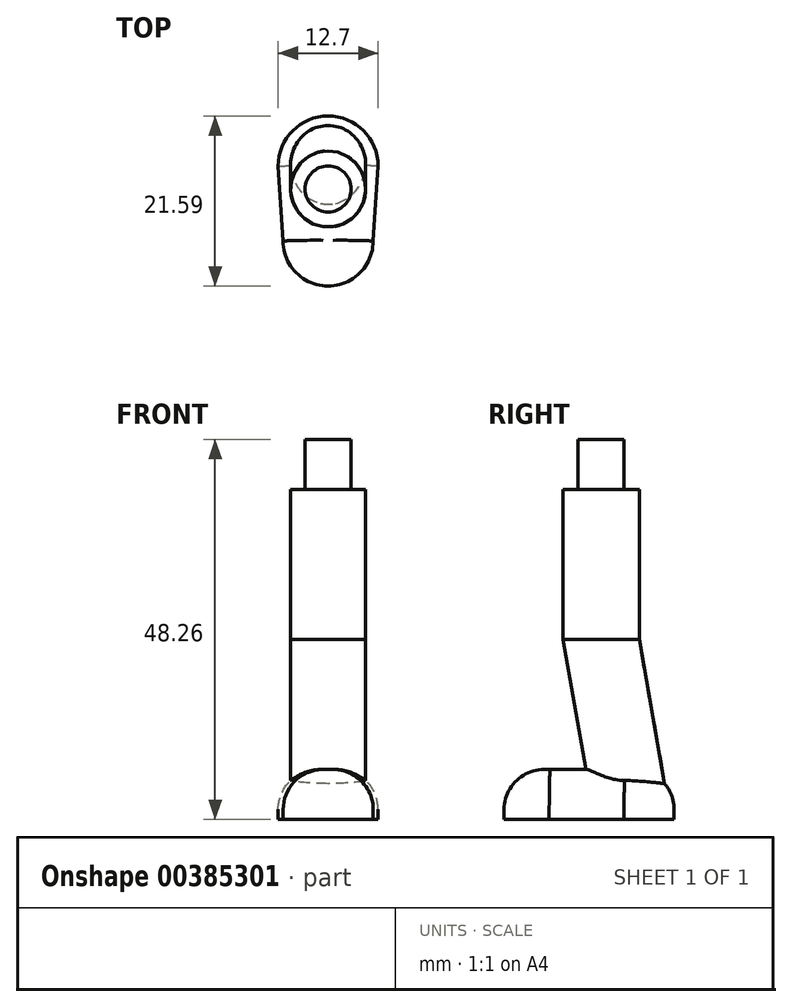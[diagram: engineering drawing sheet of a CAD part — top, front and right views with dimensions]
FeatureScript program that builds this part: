
annotation { "Feature Type Name" : "Feature", "Feature Type Description" : "" }
export const myFeature = defineFeature(function(context is Context, id is Id, definition is map)
    precondition{}
    {
        {
            var Q0;
            Q0=qCreatedBy(makeId("Top.planeOp"),FACE);
            var sketch = newSketch(context, id + "F0", { "sketchPlane" : qUnion([Q0])});
            skArc(sketch, "E0", {"start": v(6.35, 0) * mm, "mid": v(0, 6.35) * mm, "end": v(-6.35, 0) * mm});
            skLineSegment(sketch, "E1.bottom", {"start": v(-6.35, 0) * mm, "end": v(6.35, 0) * mm, "construction": true});
            skLineSegment(sketch, "E2", {"start": v(0, 0) * mm, "end": v(0, -9.53) * mm, "construction": true});
            skArc(sketch, "E3", {"start": v(-5.71, -9.5) * mm, "mid": v(0, -15.24) * mm, "end": v(5.71, -9.5) * mm});
            skLineSegment(sketch, "E4", {"start": v(-5.71, -9.5) * mm, "end": v(-6.35, 0) * mm});
            skLineSegment(sketch, "E5", {"start": v(6.35, 0) * mm, "end": v(5.71, -9.5) * mm});
            skSolve(sketch);
        }
        {
            var Q0;
            Q0 = qSketchRegion(id + "F0", true);
            extrude(context, id + "F1", {"entities" : qUnion([Q0]), "depth" : 6.35 * mm});
        }
        {
            var Q0;
            Q0=qCreatedBy(makeId("Right.planeOp"),FACE);
            var sketch = newSketch(context, id + "F2", { "sketchPlane" : qUnion([Q0])});
            skLineSegment(sketch, "E6", {"start": v(0, 6.35) * mm, "end": v(-3.3, 25.11) * mm});
            skLineSegment(sketch, "E7", {"start": v(1.53, 25.11) * mm, "end": v(4.84, 6.35) * mm});
            skLineSegment(sketch, "E8", {"start": v(4.84, 6.35) * mm, "end": v(0, 6.35) * mm});
            skLineSegment(sketch, "E9", {"start": v(-3.3, 25.11) * mm, "end": v(1.53, 25.11) * mm});
            skLineSegment(sketch, "E10", {"start": v(-3.3, 25.11) * mm, "end": v(-4.22, 30.3) * mm, "construction": true});
            skSolve(sketch);
        }
        {
            var Q0;
            Q0 = qSketchRegion(id + "F2", true);
            var Q1;
            Q1=sQuery(id+"F2.wireOp",EDGE,"E10");
            revolve(context, id + "F3", {"operationType" : NewBodyOperationType.ADD, "entities" : qUnion([Q0]), "axis" : qUnion([Q1]), "revolveType" : RevolveType.FULL});
        }
        {
            var Q0;
            Q0=qCreatedBy(makeId("Right.planeOp"),FACE);
            var sketch = newSketch(context, id + "F4", { "sketchPlane" : qUnion([Q0])});
            skLineSegment(sketch, "E11", {"start": v(-10.16, 22.86) * mm, "end": v(2.54, 22.86) * mm});
            skLineSegment(sketch, "E12", {"start": v(2.54, 22.86) * mm, "end": v(2.54, 29.21) * mm});
            skLineSegment(sketch, "E13", {"start": v(2.54, 29.21) * mm, "end": v(-10.16, 29.21) * mm});
            skLineSegment(sketch, "E14", {"start": v(-10.16, 29.21) * mm, "end": v(-10.16, 22.86) * mm});
            skSolve(sketch);
        }
        {
            var Q0;
            Q0 = qSketchRegion(id + "F4", true);
            extrude(context, id + "F5", {"entities" : qUnion([Q0]), "operationType" : NewBodyOperationType.REMOVE, "endBound" : BoundingType.SYMMETRIC, "oppositeDirection" : true, "depth" : 25.4 * mm});
        }
        {
            var Q0;
            Q0=makeQuery(id+"F5.boolean.opBoolean","COPY",FACE,{"derivedFrom":makeQuery(id+"F5.opExtrude","SWEPT_FACE",FACE,{"disambiguationData":[OSD([sQuery(id+"F4.wireOp",EDGE,"E11")])]})});
            var sketch = newSketch(context, id + "F6", { "sketchPlane" : qUnion([Q0])});
            skEllipse(sketch, "E15", {"center": v(0, -2.91) * mm, "majorRadius": 4.84 * mm, "minorRadius": 4.76 * mm, "majorAxis": v(0, 1)});
            skSolve(sketch);
        }
        {
            var Q0;
            Q0 = qSketchRegion(id + "F6", true);
            extrude(context, id + "F7", {"entities" : qUnion([Q0]), "operationType" : NewBodyOperationType.ADD, "depth" : 19.05 * mm});
        }
        {
            var Q0;
            Q0=makeQuery(id+"F7.opExtrude","CAP_FACE",FACE,{"disambiguationData":[OSD([sQuery(id+"F6.wireOp",EDGE,"E15")])],"isStart":false});
            var sketch = newSketch(context, id + "F8", { "sketchPlane" : qUnion([Q0])});
            skCircle(sketch, "E16", {"center": v(0, -2.91) * mm, "radius": 2.92 * mm});
            skSolve(sketch);
        }
        {
            var Q0;
            Q0 = qSketchRegion(id + "F8", true);
            extrude(context, id + "F9", {"entities" : qUnion([Q0]), "operationType" : NewBodyOperationType.ADD, "depth" : 6.35 * mm});
        }
        {
            var Q0;
            Q0=makeQuery(id+"F1.opExtrude","CAP_EDGE",EDGE,{"disambiguationData":[OSD([sQuery(id+"F0.wireOp",EDGE,"E0")])],"isStart":false});
            var Q1;
            Q1=makeQuery(id+"F1.opExtrude","CAP_EDGE",EDGE,{"disambiguationData":[OSD([sQuery(id+"F0.wireOp",EDGE,"E5")])],"isStart":false});
            var Q2;
            Q2=makeQuery(id+"F1.opExtrude","CAP_EDGE",EDGE,{"disambiguationData":[OSD([sQuery(id+"F0.wireOp",EDGE,"E3")])],"isStart":false});
            var Q3;
            Q3=makeQuery(id+"F1.opExtrude","CAP_EDGE",EDGE,{"disambiguationData":[OSD([sQuery(id+"F0.wireOp",EDGE,"E4")])],"isStart":false});
            fillet(context, id + "F10", {"entities" : qUnion([Q0, Q1, Q2, Q3]), "radius" : 5.08 * mm, "tangentPropagation" : true, "allowEdgeOverflow" : false});
        }
    });
